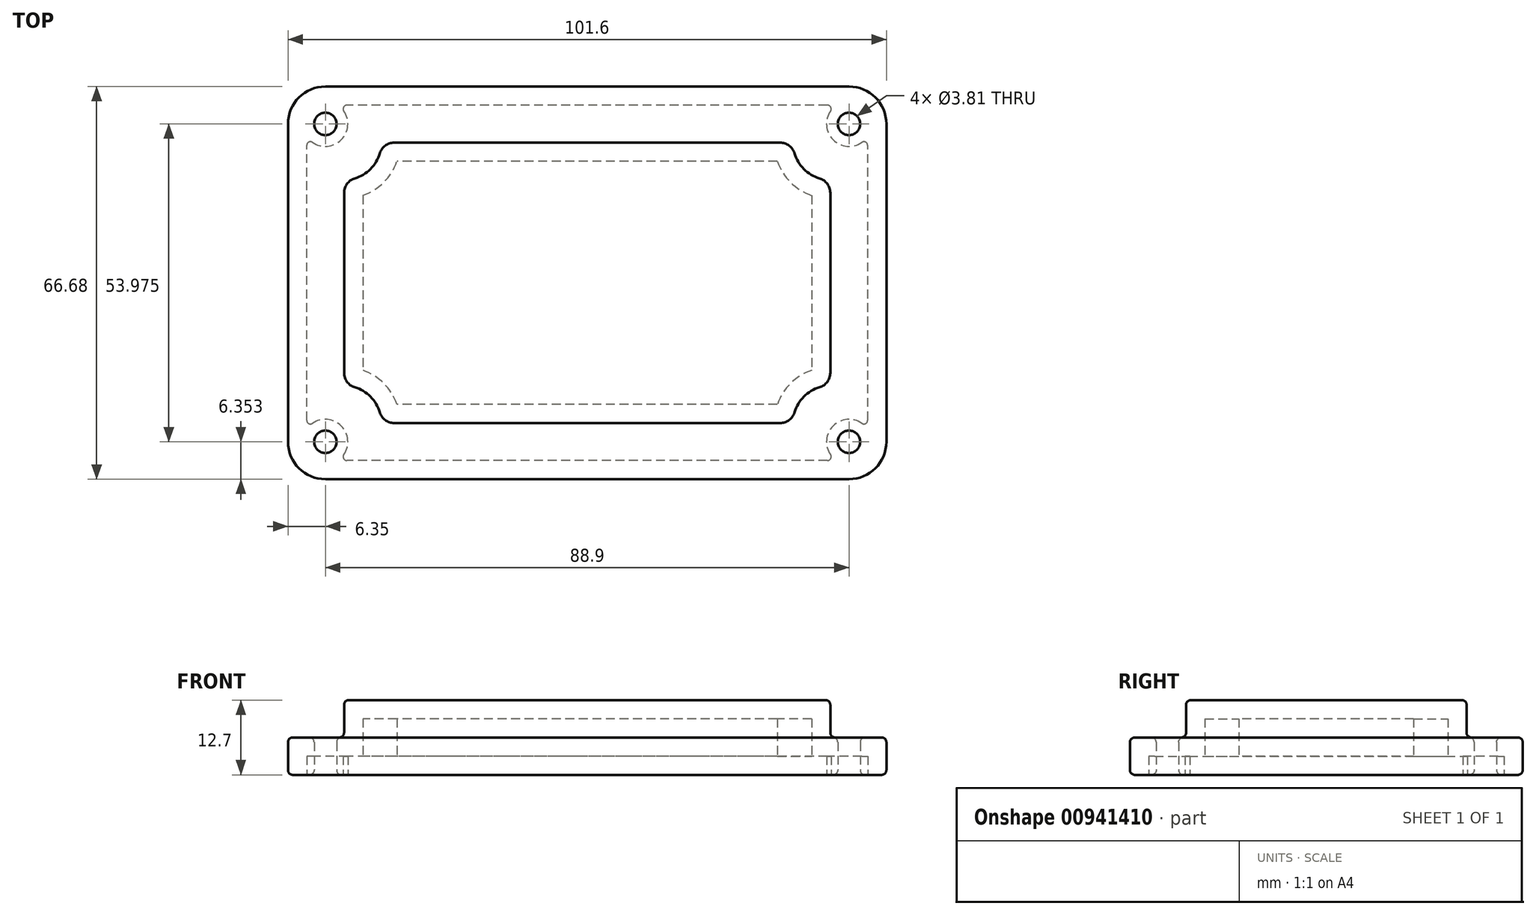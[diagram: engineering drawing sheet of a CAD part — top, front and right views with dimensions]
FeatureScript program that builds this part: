
annotation { "Feature Type Name" : "Feature", "Feature Type Description" : "" }
export const myFeature = defineFeature(function(context is Context, id is Id, definition is map)
    precondition{}
    {
        {
            var Q0;
            Q0=qCreatedBy(makeId("Top.planeOp"),FACE);
            var sketch = newSketch(context, id + "F0", { "sketchPlane" : qUnion([Q0])});
            skLineSegment(sketch, "E0.bottom", {"start": v(44.45, 33.34) * mm, "end": v(-44.45, 33.34) * mm});
            skLineSegment(sketch, "E0.top", {"start": v(44.45, -33.34) * mm, "end": v(-44.45, -33.34) * mm});
            skLineSegment(sketch, "E0.left", {"start": v(50.8, 26.99) * mm, "end": v(50.8, -26.99) * mm});
            skLineSegment(sketch, "E0.right", {"start": v(-50.8, 26.99) * mm, "end": v(-50.8, -26.99) * mm});
            skPoint(sketch, "E0.middle", {"position": v(0, 0) * mm});
            skPoint(sketch, "E1.visualSharp", {"position": v(-50.8, 33.34) * mm});
            skArc(sketch, "E1.filletArc", {"start": v(-44.45, 33.34) * mm, "mid": v(-48.94, 31.48) * mm, "end": v(-50.8, 26.99) * mm});
            skPoint(sketch, "E2.visualSharp", {"position": v(50.8, 33.34) * mm});
            skArc(sketch, "E2.filletArc", {"start": v(50.8, 26.99) * mm, "mid": v(48.94, 31.48) * mm, "end": v(44.45, 33.34) * mm});
            skPoint(sketch, "E3.visualSharp", {"position": v(50.8, -33.34) * mm});
            skArc(sketch, "E3.filletArc", {"start": v(44.45, -33.34) * mm, "mid": v(48.94, -31.48) * mm, "end": v(50.8, -26.99) * mm});
            skPoint(sketch, "E4.visualSharp", {"position": v(-50.8, -33.34) * mm});
            skArc(sketch, "E4.filletArc", {"start": v(-50.8, -26.99) * mm, "mid": v(-48.94, -31.48) * mm, "end": v(-44.45, -33.34) * mm});
            skSolve(sketch);
        }
        {
            var Q0;
            Q0 = qSketchRegion(id + "F0", true);
            extrude(context, id + "F1", {"entities" : qUnion([Q0]), "depth" : 6.35 * mm, "offsetDistance" : 25.4 * mm});
        }
        {
            var Q0;
            Q0=makeQuery(id+"F1.opExtrude","CAP_FACE",FACE,{"disambiguationData":[OSD([sQuery(id+"F0.wireOp",EDGE,"E0.bottom"),sQuery(id+"F0.wireOp",EDGE,"E0.top"),sQuery(id+"F0.wireOp",EDGE,"E0.left"),sQuery(id+"F0.wireOp",EDGE,"E0.right"),sQuery(id+"F0.wireOp",EDGE,"E1.filletArc"),sQuery(id+"F0.wireOp",EDGE,"E2.filletArc"),sQuery(id+"F0.wireOp",EDGE,"E3.filletArc"),sQuery(id+"F0.wireOp",EDGE,"E4.filletArc")])],"isStart":false});
            var sketch = newSketch(context, id + "F2", { "sketchPlane" : qUnion([Q0])});
            skLineSegment(sketch, "E5.bottom", {"start": v(32.76, 23.81) * mm, "end": v(-32.76, 23.81) * mm});
            skLineSegment(sketch, "E5.top", {"start": v(32.76, -23.81) * mm, "end": v(-32.76, -23.81) * mm});
            skLineSegment(sketch, "E5.left", {"start": v(41.28, 15.3) * mm, "end": v(41.28, -15.3) * mm});
            skLineSegment(sketch, "E5.right", {"start": v(-41.28, 15.3) * mm, "end": v(-41.28, -15.3) * mm});
            skPoint(sketch, "E5.middle", {"position": v(0, 0) * mm});
            skArc(sketch, "E6", {"start": v(-39.46, 17.73) * mm, "mid": v(-36.78, 19.32) * mm, "end": v(-35.19, 22) * mm});
            skArc(sketch, "E7", {"start": v(35.19, 22) * mm, "mid": v(36.78, 19.32) * mm, "end": v(39.46, 17.73) * mm});
            skArc(sketch, "E8", {"start": v(39.46, -17.73) * mm, "mid": v(36.78, -19.32) * mm, "end": v(35.19, -22) * mm});
            skArc(sketch, "E9", {"start": v(-35.19, -22) * mm, "mid": v(-36.78, -19.32) * mm, "end": v(-39.46, -17.73) * mm});
            skPoint(sketch, "E10.visualSharp", {"position": v(-41.28, 17.46) * mm});
            skArc(sketch, "E10.filletArc", {"start": v(-39.46, 17.73) * mm, "mid": v(-40.77, 16.81) * mm, "end": v(-41.28, 15.3) * mm});
            skPoint(sketch, "E11.visualSharp", {"position": v(-34.93, 23.81) * mm});
            skArc(sketch, "E11.filletArc", {"start": v(-32.76, 23.81) * mm, "mid": v(-34.27, 23.3) * mm, "end": v(-35.19, 22) * mm});
            skPoint(sketch, "E12.visualSharp", {"position": v(34.92, 23.81) * mm});
            skArc(sketch, "E12.filletArc", {"start": v(35.19, 22) * mm, "mid": v(34.27, 23.3) * mm, "end": v(32.76, 23.81) * mm});
            skPoint(sketch, "E13.visualSharp", {"position": v(41.28, 17.46) * mm});
            skArc(sketch, "E13.filletArc", {"start": v(41.28, 15.3) * mm, "mid": v(40.77, 16.81) * mm, "end": v(39.46, 17.73) * mm});
            skPoint(sketch, "E14.visualSharp", {"position": v(41.28, -17.46) * mm});
            skArc(sketch, "E14.filletArc", {"start": v(39.46, -17.73) * mm, "mid": v(40.77, -16.81) * mm, "end": v(41.28, -15.3) * mm});
            skPoint(sketch, "E15.visualSharp", {"position": v(34.93, -23.81) * mm});
            skArc(sketch, "E15.filletArc", {"start": v(32.76, -23.81) * mm, "mid": v(34.27, -23.3) * mm, "end": v(35.19, -22) * mm});
            skPoint(sketch, "E16.visualSharp", {"position": v(-34.93, -23.81) * mm});
            skArc(sketch, "E16.filletArc", {"start": v(-35.19, -22) * mm, "mid": v(-34.27, -23.3) * mm, "end": v(-32.76, -23.81) * mm});
            skPoint(sketch, "E17.visualSharp", {"position": v(-41.28, -17.46) * mm});
            skArc(sketch, "E17.filletArc", {"start": v(-41.27, -15.3) * mm, "mid": v(-40.77, -16.81) * mm, "end": v(-39.46, -17.73) * mm});
            skSolve(sketch);
        }
        {
            var Q0;
            Q0=makeQuery(id+"F2.imprint","IMPRINT",FACE,{"disambiguationData":[TD([[makeQuery(id+"F2.imprint","IMPRINT",EDGE,{"derivedFrom":sQuery(id+"F2.wireOp",EDGE,"E5.bottom")}),1.0]])]});
            extrude(context, id + "F3", {"entities" : qUnion([Q0]), "operationType" : NewBodyOperationType.ADD, "depth" : 6.35 * mm, "offsetDistance" : 25.4 * mm});
        }
        {
            var Q0;
            Q0=qCreatedBy(makeId("Top.planeOp"),FACE);
            var sketch = newSketch(context, id + "F4", { "sketchPlane" : qUnion([Q0])});
            skCircle(sketch, "E18", {"center": v(-44.45, 26.99) * mm, "radius": 1.9 * mm});
            skCircle(sketch, "E19", {"center": v(44.45, 26.99) * mm, "radius": 1.9 * mm});
            skCircle(sketch, "E20", {"center": v(44.45, -26.99) * mm, "radius": 1.9 * mm});
            skCircle(sketch, "E21", {"center": v(-44.45, -26.99) * mm, "radius": 1.9 * mm});
            skSolve(sketch);
        }
        {
            var Q0;
            Q0 = qSketchRegion(id + "F4", true);
            extrude(context, id + "F5", {"entities" : qUnion([Q0]), "operationType" : NewBodyOperationType.REMOVE, "endBound" : BoundingType.THROUGH_ALL, "depth" : 6.35 * mm, "offsetDistance" : 25.4 * mm});
        }
        {
            var Q0;
            Q0=makeQuery(id+"F1.opExtrude","CAP_FACE",FACE,{"disambiguationData":[OSD([sQuery(id+"F0.wireOp",EDGE,"E0.bottom"),sQuery(id+"F0.wireOp",EDGE,"E0.top"),sQuery(id+"F0.wireOp",EDGE,"E0.left"),sQuery(id+"F0.wireOp",EDGE,"E0.right"),sQuery(id+"F0.wireOp",EDGE,"E1.filletArc"),sQuery(id+"F0.wireOp",EDGE,"E2.filletArc"),sQuery(id+"F0.wireOp",EDGE,"E3.filletArc"),sQuery(id+"F0.wireOp",EDGE,"E4.filletArc")])],"isStart":false});
            var Q1;
            Q1=makeQuery(id+"F3.opExtrude","SWEPT_FACE",FACE,{"disambiguationData":[OSD([sQuery(id+"F2.wireOp",EDGE,"E15.filletArc")])]});
            var Q2;
            Q2=makeQuery(id+"F3.opExtrude","SWEPT_FACE",FACE,{"disambiguationData":[OSD([sQuery(id+"F2.wireOp",EDGE,"E13.filletArc")])]});
            var Q3;
            Q3=makeQuery(id+"F3.opExtrude","SWEPT_FACE",FACE,{"disambiguationData":[OSD([sQuery(id+"F2.wireOp",EDGE,"E14.filletArc")])]});
            var Q4;
            Q4=makeQuery(id+"F3.opExtrude","SWEPT_FACE",FACE,{"disambiguationData":[OSD([sQuery(id+"F2.wireOp",EDGE,"E5.bottom")])]});
            var Q5;
            Q5=makeQuery(id+"F3.opExtrude","CAP_FACE",FACE,{"disambiguationData":[OSD([sQuery(id+"F2.wireOp",EDGE,"E5.bottom"),sQuery(id+"F2.wireOp",EDGE,"E5.top"),sQuery(id+"F2.wireOp",EDGE,"E5.left"),sQuery(id+"F2.wireOp",EDGE,"E5.right"),sQuery(id+"F2.wireOp",EDGE,"E6"),sQuery(id+"F2.wireOp",EDGE,"E7"),sQuery(id+"F2.wireOp",EDGE,"E8"),sQuery(id+"F2.wireOp",EDGE,"E9"),sQuery(id+"F2.wireOp",EDGE,"E10.filletArc"),sQuery(id+"F2.wireOp",EDGE,"E11.filletArc"),sQuery(id+"F2.wireOp",EDGE,"E12.filletArc"),sQuery(id+"F2.wireOp",EDGE,"E13.filletArc"),sQuery(id+"F2.wireOp",EDGE,"E14.filletArc"),sQuery(id+"F2.wireOp",EDGE,"E15.filletArc"),sQuery(id+"F2.wireOp",EDGE,"E16.filletArc"),sQuery(id+"F2.wireOp",EDGE,"E17.filletArc")])],"isStart":false});
            var Q6;
            Q6=makeQuery(id+"F3.opExtrude","SWEPT_FACE",FACE,{"disambiguationData":[OSD([sQuery(id+"F2.wireOp",EDGE,"E5.top")])]});
            var Q7;
            Q7=makeQuery(id+"F3.opExtrude","SWEPT_FACE",FACE,{"disambiguationData":[OSD([sQuery(id+"F2.wireOp",EDGE,"E5.left")])]});
            var Q8;
            Q8=makeQuery(id+"F3.opExtrude","SWEPT_FACE",FACE,{"disambiguationData":[OSD([sQuery(id+"F2.wireOp",EDGE,"E5.right")])]});
            var Q9;
            Q9=makeQuery(id+"F3.opExtrude","SWEPT_FACE",FACE,{"disambiguationData":[OSD([sQuery(id+"F2.wireOp",EDGE,"E9")])]});
            var Q10;
            Q10=makeQuery(id+"F3.opExtrude","SWEPT_FACE",FACE,{"disambiguationData":[OSD([sQuery(id+"F2.wireOp",EDGE,"E10.filletArc")])]});
            var Q11;
            Q11=makeQuery(id+"F3.opExtrude","SWEPT_FACE",FACE,{"disambiguationData":[OSD([sQuery(id+"F2.wireOp",EDGE,"E11.filletArc")])]});
            var Q12;
            Q12=makeQuery(id+"F3.opExtrude","SWEPT_FACE",FACE,{"disambiguationData":[OSD([sQuery(id+"F2.wireOp",EDGE,"E12.filletArc")])]});
            var Q13;
            Q13=makeQuery(id+"F3.opExtrude","CAP_EDGE",EDGE,{"disambiguationData":[OSD([sQuery(id+"F2.wireOp",EDGE,"E8")])],"isStart":false});
            var Q14;
            Q14=makeQuery(id+"F3.opExtrude","CAP_EDGE",EDGE,{"disambiguationData":[OSD([sQuery(id+"F2.wireOp",EDGE,"E9")])],"isStart":false});
            var Q15;
            Q15=makeQuery(id+"F3.opExtrude","SWEPT_FACE",FACE,{"disambiguationData":[OSD([sQuery(id+"F2.wireOp",EDGE,"E16.filletArc")])]});
            var Q16;
            Q16=makeQuery(id+"F3.opExtrude","SWEPT_FACE",FACE,{"disambiguationData":[OSD([sQuery(id+"F2.wireOp",EDGE,"E17.filletArc")])]});
            var Q17;
            Q17=makeQuery(id+"F1.opExtrude","SWEPT_FACE",FACE,{"disambiguationData":[OSD([sQuery(id+"F0.wireOp",EDGE,"E0.bottom")])]});
            var Q18;
            Q18=makeQuery(id+"F1.opExtrude","SWEPT_FACE",FACE,{"disambiguationData":[OSD([sQuery(id+"F0.wireOp",EDGE,"E0.top")])]});
            var Q19;
            Q19=makeQuery(id+"F1.opExtrude","SWEPT_FACE",FACE,{"disambiguationData":[OSD([sQuery(id+"F0.wireOp",EDGE,"E0.left")])]});
            var Q20;
            Q20=makeQuery(id+"F1.opExtrude","SWEPT_FACE",FACE,{"disambiguationData":[OSD([sQuery(id+"F0.wireOp",EDGE,"E0.right")])]});
            var Q21;
            Q21=makeQuery(id+"F1.opExtrude","SWEPT_FACE",FACE,{"disambiguationData":[OSD([sQuery(id+"F0.wireOp",EDGE,"E1.filletArc")])]});
            var Q22;
            Q22=makeQuery(id+"F1.opExtrude","SWEPT_FACE",FACE,{"disambiguationData":[OSD([sQuery(id+"F0.wireOp",EDGE,"E2.filletArc")])]});
            var Q23;
            Q23=makeQuery(id+"F1.opExtrude","SWEPT_FACE",FACE,{"disambiguationData":[OSD([sQuery(id+"F0.wireOp",EDGE,"E3.filletArc")])]});
            var Q24;
            Q24=makeQuery(id+"F1.opExtrude","SWEPT_FACE",FACE,{"disambiguationData":[OSD([sQuery(id+"F0.wireOp",EDGE,"E4.filletArc")])]});
            var Q25;
            Q25=makeQuery(id+"F5.boolean.opBoolean","INTERSECT",EDGE,{"derivedFrom":[makeQuery(id+"F1.opExtrude","CAP_FACE",FACE,{"disambiguationData":[OSD([sQuery(id+"F0.wireOp",EDGE,"E0.bottom"),sQuery(id+"F0.wireOp",EDGE,"E0.top"),sQuery(id+"F0.wireOp",EDGE,"E0.left"),sQuery(id+"F0.wireOp",EDGE,"E0.right"),sQuery(id+"F0.wireOp",EDGE,"E1.filletArc"),sQuery(id+"F0.wireOp",EDGE,"E2.filletArc"),sQuery(id+"F0.wireOp",EDGE,"E3.filletArc"),sQuery(id+"F0.wireOp",EDGE,"E4.filletArc")])],"isStart":false}),makeQuery(id+"F5.opExtrude","SWEPT_FACE",FACE,{"disambiguationData":[OSD([sQuery(id+"F4.wireOp",EDGE,"E21")])]})]});
            var Q26;
            Q26=makeQuery(id+"F5.boolean.opBoolean","INTERSECT",EDGE,{"derivedFrom":[makeQuery(id+"F1.opExtrude","CAP_FACE",FACE,{"disambiguationData":[OSD([sQuery(id+"F0.wireOp",EDGE,"E0.bottom"),sQuery(id+"F0.wireOp",EDGE,"E0.top"),sQuery(id+"F0.wireOp",EDGE,"E0.left"),sQuery(id+"F0.wireOp",EDGE,"E0.right"),sQuery(id+"F0.wireOp",EDGE,"E1.filletArc"),sQuery(id+"F0.wireOp",EDGE,"E2.filletArc"),sQuery(id+"F0.wireOp",EDGE,"E3.filletArc"),sQuery(id+"F0.wireOp",EDGE,"E4.filletArc")])],"isStart":false}),makeQuery(id+"F5.opExtrude","SWEPT_FACE",FACE,{"disambiguationData":[OSD([sQuery(id+"F4.wireOp",EDGE,"E20")])]})]});
            var Q27;
            Q27=makeQuery(id+"F5.boolean.opBoolean","INTERSECT",EDGE,{"derivedFrom":[makeQuery(id+"F1.opExtrude","CAP_FACE",FACE,{"disambiguationData":[OSD([sQuery(id+"F0.wireOp",EDGE,"E0.bottom"),sQuery(id+"F0.wireOp",EDGE,"E0.top"),sQuery(id+"F0.wireOp",EDGE,"E0.left"),sQuery(id+"F0.wireOp",EDGE,"E0.right"),sQuery(id+"F0.wireOp",EDGE,"E1.filletArc"),sQuery(id+"F0.wireOp",EDGE,"E2.filletArc"),sQuery(id+"F0.wireOp",EDGE,"E3.filletArc"),sQuery(id+"F0.wireOp",EDGE,"E4.filletArc")])],"isStart":false}),makeQuery(id+"F5.opExtrude","SWEPT_FACE",FACE,{"disambiguationData":[OSD([sQuery(id+"F4.wireOp",EDGE,"E19")])]})]});
            var Q28;
            Q28=makeQuery(id+"F1.opExtrude","CAP_FACE",FACE,{"disambiguationData":[OSD([sQuery(id+"F0.wireOp",EDGE,"E0.bottom"),sQuery(id+"F0.wireOp",EDGE,"E0.top"),sQuery(id+"F0.wireOp",EDGE,"E0.left"),sQuery(id+"F0.wireOp",EDGE,"E0.right"),sQuery(id+"F0.wireOp",EDGE,"E1.filletArc"),sQuery(id+"F0.wireOp",EDGE,"E2.filletArc"),sQuery(id+"F0.wireOp",EDGE,"E3.filletArc"),sQuery(id+"F0.wireOp",EDGE,"E4.filletArc")])],"isStart":true});
            var Q29;
            Q29=makeQuery(id+"F5.boolean.opBoolean","INTERSECT",EDGE,{"derivedFrom":[makeQuery(id+"F1.opExtrude","CAP_FACE",FACE,{"disambiguationData":[OSD([sQuery(id+"F0.wireOp",EDGE,"E0.bottom"),sQuery(id+"F0.wireOp",EDGE,"E0.top"),sQuery(id+"F0.wireOp",EDGE,"E0.left"),sQuery(id+"F0.wireOp",EDGE,"E0.right"),sQuery(id+"F0.wireOp",EDGE,"E1.filletArc"),sQuery(id+"F0.wireOp",EDGE,"E2.filletArc"),sQuery(id+"F0.wireOp",EDGE,"E3.filletArc"),sQuery(id+"F0.wireOp",EDGE,"E4.filletArc")])],"isStart":false}),makeQuery(id+"F5.opExtrude","SWEPT_FACE",FACE,{"disambiguationData":[OSD([sQuery(id+"F4.wireOp",EDGE,"E18")])]})]});
            var Q30;
            Q30=makeQuery(id+"F5.boolean.opBoolean","COPY",FACE,{"derivedFrom":makeQuery(id+"F5.opExtrude","SWEPT_FACE",FACE,{"disambiguationData":[OSD([sQuery(id+"F4.wireOp",EDGE,"E19")])]})});
            var Q31;
            Q31=makeQuery(id+"F1.opExtrude","CAP_EDGE",EDGE,{"disambiguationData":[OSD([sQuery(id+"F0.wireOp",EDGE,"E1.filletArc")])],"isStart":false});
            var Q32;
            Q32=makeQuery(id+"F1.opExtrude","CAP_EDGE",EDGE,{"disambiguationData":[OSD([sQuery(id+"F0.wireOp",EDGE,"E2.filletArc")])],"isStart":false});
            var Q33;
            Q33=makeQuery(id+"F1.opExtrude","CAP_EDGE",EDGE,{"disambiguationData":[OSD([sQuery(id+"F0.wireOp",EDGE,"E3.filletArc")])],"isStart":false});
            var Q34;
            Q34=makeQuery(id+"F1.opExtrude","CAP_EDGE",EDGE,{"disambiguationData":[OSD([sQuery(id+"F0.wireOp",EDGE,"E4.filletArc")])],"isStart":false});
            var Q35;
            Q35=makeQuery(id+"F3.opExtrude","CAP_FACE",FACE,{"disambiguationData":[OSD([sQuery(id+"F2.wireOp",EDGE,"E5.bottom"),sQuery(id+"F2.wireOp",EDGE,"E5.top"),sQuery(id+"F2.wireOp",EDGE,"E5.left"),sQuery(id+"F2.wireOp",EDGE,"E5.right"),sQuery(id+"F2.wireOp",EDGE,"E6"),sQuery(id+"F2.wireOp",EDGE,"E7"),sQuery(id+"F2.wireOp",EDGE,"E8"),sQuery(id+"F2.wireOp",EDGE,"E9"),sQuery(id+"F2.wireOp",EDGE,"E10.filletArc"),sQuery(id+"F2.wireOp",EDGE,"E11.filletArc"),sQuery(id+"F2.wireOp",EDGE,"E12.filletArc"),sQuery(id+"F2.wireOp",EDGE,"E13.filletArc"),sQuery(id+"F2.wireOp",EDGE,"E14.filletArc"),sQuery(id+"F2.wireOp",EDGE,"E15.filletArc"),sQuery(id+"F2.wireOp",EDGE,"E16.filletArc"),sQuery(id+"F2.wireOp",EDGE,"E17.filletArc")])],"isStart":true});
            var Q36;
            Q36=makeQuery(id+"F3.opExtrude","SWEPT_FACE",FACE,{"disambiguationData":[OSD([sQuery(id+"F2.wireOp",EDGE,"E8")])]});
            var Q37;
            Q37=makeQuery(id+"F3.opExtrude","CAP_EDGE",EDGE,{"disambiguationData":[OSD([sQuery(id+"F2.wireOp",EDGE,"E16.filletArc")])],"isStart":false});
            var Q38;
            Q38=makeQuery(id+"F3.opExtrude","CAP_EDGE",EDGE,{"disambiguationData":[OSD([sQuery(id+"F2.wireOp",EDGE,"E9")])],"isStart":true});
            var Q39;
            Q39=makeQuery(id+"F3.opExtrude","CAP_EDGE",EDGE,{"disambiguationData":[OSD([sQuery(id+"F2.wireOp",EDGE,"E17.filletArc")])],"isStart":false});
            var Q40;
            Q40=makeQuery(id+"F3.opExtrude","CAP_EDGE",EDGE,{"disambiguationData":[OSD([sQuery(id+"F2.wireOp",EDGE,"E5.bottom")])],"isStart":false});
            var Q41;
            Q41=makeQuery(id+"F3.opExtrude","CAP_EDGE",EDGE,{"disambiguationData":[OSD([sQuery(id+"F2.wireOp",EDGE,"E10.filletArc")])],"isStart":false});
            var Q42;
            Q42=makeQuery(id+"F3.opExtrude","CAP_EDGE",EDGE,{"disambiguationData":[OSD([sQuery(id+"F2.wireOp",EDGE,"E5.top")])],"isStart":false});
            var Q43;
            Q43=makeQuery(id+"F3.opExtrude","CAP_EDGE",EDGE,{"disambiguationData":[OSD([sQuery(id+"F2.wireOp",EDGE,"E11.filletArc")])],"isStart":false});
            var Q44;
            Q44=makeQuery(id+"F3.opExtrude","CAP_EDGE",EDGE,{"disambiguationData":[OSD([sQuery(id+"F2.wireOp",EDGE,"E5.left")])],"isStart":false});
            var Q45;
            Q45=makeQuery(id+"F3.opExtrude","CAP_EDGE",EDGE,{"disambiguationData":[OSD([sQuery(id+"F2.wireOp",EDGE,"E12.filletArc")])],"isStart":false});
            var Q46;
            Q46=makeQuery(id+"F3.opExtrude","CAP_EDGE",EDGE,{"disambiguationData":[OSD([sQuery(id+"F2.wireOp",EDGE,"E5.right")])],"isStart":false});
            var Q47;
            Q47=makeQuery(id+"F3.opExtrude","CAP_EDGE",EDGE,{"disambiguationData":[OSD([sQuery(id+"F2.wireOp",EDGE,"E13.filletArc")])],"isStart":false});
            var Q48;
            Q48=makeQuery(id+"F3.opExtrude","CAP_EDGE",EDGE,{"disambiguationData":[OSD([sQuery(id+"F2.wireOp",EDGE,"E6")])],"isStart":false});
            var Q49;
            Q49=makeQuery(id+"F3.opExtrude","CAP_EDGE",EDGE,{"disambiguationData":[OSD([sQuery(id+"F2.wireOp",EDGE,"E14.filletArc")])],"isStart":false});
            var Q50;
            Q50=makeQuery(id+"F3.opExtrude","CAP_EDGE",EDGE,{"disambiguationData":[OSD([sQuery(id+"F2.wireOp",EDGE,"E7")])],"isStart":false});
            var Q51;
            Q51=makeQuery(id+"F3.opExtrude","CAP_EDGE",EDGE,{"disambiguationData":[OSD([sQuery(id+"F2.wireOp",EDGE,"E15.filletArc")])],"isStart":false});
            var Q52;
            Q52=makeQuery(id+"F1.opExtrude","CAP_EDGE",EDGE,{"disambiguationData":[OSD([sQuery(id+"F0.wireOp",EDGE,"E0.left")])],"isStart":false});
            var Q53;
            Q53=makeQuery(id+"F1.opExtrude","CAP_EDGE",EDGE,{"disambiguationData":[OSD([sQuery(id+"F0.wireOp",EDGE,"E0.right")])],"isStart":false});
            var Q54;
            Q54=makeQuery(id+"F1.opExtrude","CAP_EDGE",EDGE,{"disambiguationData":[OSD([sQuery(id+"F0.wireOp",EDGE,"E0.bottom")])],"isStart":false});
            var Q55;
            Q55=makeQuery(id+"F1.opExtrude","CAP_EDGE",EDGE,{"disambiguationData":[OSD([sQuery(id+"F0.wireOp",EDGE,"E0.top")])],"isStart":false});
            var Q56;
            Q56=makeQuery(id+"F5.boolean.opBoolean","COPY",FACE,{"derivedFrom":makeQuery(id+"F5.opExtrude","SWEPT_FACE",FACE,{"disambiguationData":[OSD([sQuery(id+"F4.wireOp",EDGE,"E21")])]})});
            var Q57;
            Q57=makeQuery(id+"F5.boolean.opBoolean","COPY",FACE,{"derivedFrom":makeQuery(id+"F5.opExtrude","SWEPT_FACE",FACE,{"disambiguationData":[OSD([sQuery(id+"F4.wireOp",EDGE,"E20")])]})});
            var Q58;
            Q58=makeQuery(id+"F5.boolean.opBoolean","COPY",EDGE,{"derivedFrom":makeQuery(id+"F5.opExtrude","CAP_EDGE",EDGE,{"disambiguationData":[OSD([sQuery(id+"F4.wireOp",EDGE,"E19")])],"isStart":true})});
            var Q59;
            Q59=makeQuery(id+"F1.opExtrude","CAP_EDGE",EDGE,{"disambiguationData":[OSD([sQuery(id+"F0.wireOp",EDGE,"E1.filletArc")])],"isStart":true});
            var Q60;
            Q60=makeQuery(id+"F1.opExtrude","CAP_EDGE",EDGE,{"disambiguationData":[OSD([sQuery(id+"F0.wireOp",EDGE,"E2.filletArc")])],"isStart":true});
            var Q61;
            Q61=makeQuery(id+"F1.opExtrude","CAP_EDGE",EDGE,{"disambiguationData":[OSD([sQuery(id+"F0.wireOp",EDGE,"E3.filletArc")])],"isStart":true});
            var Q62;
            Q62=makeQuery(id+"F1.opExtrude","CAP_EDGE",EDGE,{"disambiguationData":[OSD([sQuery(id+"F0.wireOp",EDGE,"E4.filletArc")])],"isStart":true});
            var Q63;
            Q63=makeQuery(id+"F5.boolean.opBoolean","COPY",FACE,{"derivedFrom":makeQuery(id+"F5.opExtrude","SWEPT_FACE",FACE,{"disambiguationData":[OSD([sQuery(id+"F4.wireOp",EDGE,"E18")])]})});
            var Q64;
            Q64=makeQuery(id+"F3.opExtrude","SWEPT_EDGE",EDGE,{"disambiguationData":[OSD([sQuery(id+"F2.wireOp",EDGE,"E8"),sQuery(id+"F2.wireOp",EDGE,"E15.filletArc")])]});
            var Q65;
            Q65=makeQuery(id+"F3.opExtrude","SWEPT_EDGE",EDGE,{"disambiguationData":[OSD([sQuery(id+"F2.wireOp",EDGE,"E9"),sQuery(id+"F2.wireOp",EDGE,"E16.filletArc")])]});
            var Q66;
            Q66=makeQuery(id+"F3.opExtrude","SWEPT_EDGE",EDGE,{"disambiguationData":[OSD([sQuery(id+"F2.wireOp",EDGE,"E9"),sQuery(id+"F2.wireOp",EDGE,"E17.filletArc")])]});
            var Q67;
            Q67=makeQuery(id+"F3.opExtrude","SWEPT_EDGE",EDGE,{"disambiguationData":[OSD([sQuery(id+"F2.wireOp",EDGE,"E5.bottom"),sQuery(id+"F2.wireOp",EDGE,"E12.filletArc")])]});
            var Q68;
            Q68=makeQuery(id+"F3.opExtrude","SWEPT_EDGE",EDGE,{"disambiguationData":[OSD([sQuery(id+"F2.wireOp",EDGE,"E5.bottom"),sQuery(id+"F2.wireOp",EDGE,"E11.filletArc")])]});
            var Q69;
            Q69=makeQuery(id+"F3.opExtrude","SWEPT_EDGE",EDGE,{"disambiguationData":[OSD([sQuery(id+"F2.wireOp",EDGE,"E5.top"),sQuery(id+"F2.wireOp",EDGE,"E15.filletArc")])]});
            var Q70;
            Q70=makeQuery(id+"F3.opExtrude","SWEPT_EDGE",EDGE,{"disambiguationData":[OSD([sQuery(id+"F2.wireOp",EDGE,"E5.top"),sQuery(id+"F2.wireOp",EDGE,"E16.filletArc")])]});
            var Q71;
            Q71=makeQuery(id+"F3.opExtrude","SWEPT_EDGE",EDGE,{"disambiguationData":[OSD([sQuery(id+"F2.wireOp",EDGE,"E5.left"),sQuery(id+"F2.wireOp",EDGE,"E13.filletArc")])]});
            var Q72;
            Q72=makeQuery(id+"F3.opExtrude","SWEPT_EDGE",EDGE,{"disambiguationData":[OSD([sQuery(id+"F2.wireOp",EDGE,"E5.left"),sQuery(id+"F2.wireOp",EDGE,"E14.filletArc")])]});
            var Q73;
            Q73=makeQuery(id+"F3.opExtrude","SWEPT_EDGE",EDGE,{"disambiguationData":[OSD([sQuery(id+"F2.wireOp",EDGE,"E5.right"),sQuery(id+"F2.wireOp",EDGE,"E10.filletArc")])]});
            var Q74;
            Q74=makeQuery(id+"F3.opExtrude","SWEPT_FACE",FACE,{"disambiguationData":[OSD([sQuery(id+"F2.wireOp",EDGE,"E6")])]});
            var Q75;
            Q75=makeQuery(id+"F3.opExtrude","SWEPT_EDGE",EDGE,{"disambiguationData":[OSD([sQuery(id+"F2.wireOp",EDGE,"E5.right"),sQuery(id+"F2.wireOp",EDGE,"E17.filletArc")])]});
            var Q76;
            Q76=makeQuery(id+"F3.opExtrude","SWEPT_FACE",FACE,{"disambiguationData":[OSD([sQuery(id+"F2.wireOp",EDGE,"E7")])]});
            var Q77;
            Q77=makeQuery(id+"F3.opExtrude","SWEPT_EDGE",EDGE,{"disambiguationData":[OSD([sQuery(id+"F2.wireOp",EDGE,"E6"),sQuery(id+"F2.wireOp",EDGE,"E10.filletArc")])]});
            var Q78;
            Q78=makeQuery(id+"F3.opExtrude","SWEPT_EDGE",EDGE,{"disambiguationData":[OSD([sQuery(id+"F2.wireOp",EDGE,"E6"),sQuery(id+"F2.wireOp",EDGE,"E11.filletArc")])]});
            var Q79;
            Q79=makeQuery(id+"F3.opExtrude","SWEPT_EDGE",EDGE,{"disambiguationData":[OSD([sQuery(id+"F2.wireOp",EDGE,"E7"),sQuery(id+"F2.wireOp",EDGE,"E12.filletArc")])]});
            var Q80;
            Q80=makeQuery(id+"F3.opExtrude","SWEPT_EDGE",EDGE,{"disambiguationData":[OSD([sQuery(id+"F2.wireOp",EDGE,"E7"),sQuery(id+"F2.wireOp",EDGE,"E13.filletArc")])]});
            var Q81;
            Q81=makeQuery(id+"F3.opExtrude","SWEPT_EDGE",EDGE,{"disambiguationData":[OSD([sQuery(id+"F2.wireOp",EDGE,"E8"),sQuery(id+"F2.wireOp",EDGE,"E14.filletArc")])]});
            var Q82;
            Q82=makeQuery(id+"F3.opExtrude","CAP_EDGE",EDGE,{"disambiguationData":[OSD([sQuery(id+"F2.wireOp",EDGE,"E17.filletArc")])],"isStart":true});
            var Q83;
            Q83=makeQuery(id+"F3.opExtrude","CAP_EDGE",EDGE,{"disambiguationData":[OSD([sQuery(id+"F2.wireOp",EDGE,"E5.bottom")])],"isStart":true});
            var Q84;
            Q84=makeQuery(id+"F3.opExtrude","CAP_EDGE",EDGE,{"disambiguationData":[OSD([sQuery(id+"F2.wireOp",EDGE,"E10.filletArc")])],"isStart":true});
            var Q85;
            Q85=makeQuery(id+"F3.opExtrude","CAP_EDGE",EDGE,{"disambiguationData":[OSD([sQuery(id+"F2.wireOp",EDGE,"E5.top")])],"isStart":true});
            var Q86;
            Q86=makeQuery(id+"F3.opExtrude","CAP_EDGE",EDGE,{"disambiguationData":[OSD([sQuery(id+"F2.wireOp",EDGE,"E11.filletArc")])],"isStart":true});
            var Q87;
            Q87=makeQuery(id+"F3.opExtrude","CAP_EDGE",EDGE,{"disambiguationData":[OSD([sQuery(id+"F2.wireOp",EDGE,"E5.left")])],"isStart":true});
            var Q88;
            Q88=makeQuery(id+"F3.opExtrude","CAP_EDGE",EDGE,{"disambiguationData":[OSD([sQuery(id+"F2.wireOp",EDGE,"E12.filletArc")])],"isStart":true});
            var Q89;
            Q89=makeQuery(id+"F3.opExtrude","CAP_EDGE",EDGE,{"disambiguationData":[OSD([sQuery(id+"F2.wireOp",EDGE,"E5.right")])],"isStart":true});
            var Q90;
            Q90=makeQuery(id+"F3.opExtrude","CAP_EDGE",EDGE,{"disambiguationData":[OSD([sQuery(id+"F2.wireOp",EDGE,"E13.filletArc")])],"isStart":true});
            var Q91;
            Q91=makeQuery(id+"F3.opExtrude","CAP_EDGE",EDGE,{"disambiguationData":[OSD([sQuery(id+"F2.wireOp",EDGE,"E14.filletArc")])],"isStart":true});
            var Q92;
            Q92=makeQuery(id+"F3.opExtrude","CAP_EDGE",EDGE,{"disambiguationData":[OSD([sQuery(id+"F2.wireOp",EDGE,"E15.filletArc")])],"isStart":true});
            var Q93;
            Q93=makeQuery(id+"F3.opExtrude","CAP_EDGE",EDGE,{"disambiguationData":[OSD([sQuery(id+"F2.wireOp",EDGE,"E8")])],"isStart":true});
            var Q94;
            Q94=makeQuery(id+"F3.opExtrude","CAP_EDGE",EDGE,{"disambiguationData":[OSD([sQuery(id+"F2.wireOp",EDGE,"E16.filletArc")])],"isStart":true});
            var Q95;
            Q95=makeQuery(id+"F1.opExtrude","CAP_EDGE",EDGE,{"disambiguationData":[OSD([sQuery(id+"F0.wireOp",EDGE,"E0.right")])],"isStart":true});
            var Q96;
            Q96=makeQuery(id+"F1.opExtrude","SWEPT_EDGE",EDGE,{"disambiguationData":[OSD([sQuery(id+"F0.wireOp",EDGE,"E0.bottom"),sQuery(id+"F0.wireOp",EDGE,"E2.filletArc")])]});
            var Q97;
            Q97=makeQuery(id+"F1.opExtrude","SWEPT_EDGE",EDGE,{"disambiguationData":[OSD([sQuery(id+"F0.wireOp",EDGE,"E0.bottom"),sQuery(id+"F0.wireOp",EDGE,"E1.filletArc")])]});
            var Q98;
            Q98=makeQuery(id+"F1.opExtrude","SWEPT_EDGE",EDGE,{"disambiguationData":[OSD([sQuery(id+"F0.wireOp",EDGE,"E0.top"),sQuery(id+"F0.wireOp",EDGE,"E3.filletArc")])]});
            var Q99;
            Q99=makeQuery(id+"F5.boolean.opBoolean","COPY",EDGE,{"derivedFrom":makeQuery(id+"F5.opExtrude","CAP_EDGE",EDGE,{"disambiguationData":[OSD([sQuery(id+"F4.wireOp",EDGE,"E18")])],"isStart":true})});
            var Q100;
            Q100=makeQuery(id+"F1.opExtrude","SWEPT_EDGE",EDGE,{"disambiguationData":[OSD([sQuery(id+"F0.wireOp",EDGE,"E0.top"),sQuery(id+"F0.wireOp",EDGE,"E4.filletArc")])]});
            var Q101;
            Q101=makeQuery(id+"F1.opExtrude","SWEPT_EDGE",EDGE,{"disambiguationData":[OSD([sQuery(id+"F0.wireOp",EDGE,"E0.left"),sQuery(id+"F0.wireOp",EDGE,"E2.filletArc")])]});
            var Q102;
            Q102=makeQuery(id+"F1.opExtrude","SWEPT_EDGE",EDGE,{"disambiguationData":[OSD([sQuery(id+"F0.wireOp",EDGE,"E0.left"),sQuery(id+"F0.wireOp",EDGE,"E3.filletArc")])]});
            var Q103;
            Q103=makeQuery(id+"F1.opExtrude","SWEPT_EDGE",EDGE,{"disambiguationData":[OSD([sQuery(id+"F0.wireOp",EDGE,"E0.right"),sQuery(id+"F0.wireOp",EDGE,"E1.filletArc")])]});
            var Q104;
            Q104=makeQuery(id+"F1.opExtrude","SWEPT_EDGE",EDGE,{"disambiguationData":[OSD([sQuery(id+"F0.wireOp",EDGE,"E0.right"),sQuery(id+"F0.wireOp",EDGE,"E4.filletArc")])]});
            var Q105;
            Q105=makeQuery(id+"F1.opExtrude","CAP_EDGE",EDGE,{"disambiguationData":[OSD([sQuery(id+"F0.wireOp",EDGE,"E0.bottom")])],"isStart":true});
            var Q106;
            Q106=makeQuery(id+"F1.opExtrude","CAP_EDGE",EDGE,{"disambiguationData":[OSD([sQuery(id+"F0.wireOp",EDGE,"E0.top")])],"isStart":true});
            var Q107;
            Q107=makeQuery(id+"F1.opExtrude","CAP_EDGE",EDGE,{"disambiguationData":[OSD([sQuery(id+"F0.wireOp",EDGE,"E0.left")])],"isStart":true});
            var Q108;
            Q108=makeQuery(id+"F5.boolean.opBoolean","COPY",EDGE,{"derivedFrom":makeQuery(id+"F5.opExtrude","CAP_EDGE",EDGE,{"disambiguationData":[OSD([sQuery(id+"F4.wireOp",EDGE,"E21")])],"isStart":true})});
            var Q109;
            Q109=makeQuery(id+"F5.boolean.opBoolean","COPY",EDGE,{"derivedFrom":makeQuery(id+"F5.opExtrude","CAP_EDGE",EDGE,{"disambiguationData":[OSD([sQuery(id+"F4.wireOp",EDGE,"E20")])],"isStart":true})});
            var Q110;
            Q110=makeQuery(id+"F3.opExtrude","CAP_EDGE",EDGE,{"disambiguationData":[OSD([sQuery(id+"F2.wireOp",EDGE,"E6")])],"isStart":true});
            var Q111;
            Q111=makeQuery(id+"F3.opExtrude","CAP_EDGE",EDGE,{"disambiguationData":[OSD([sQuery(id+"F2.wireOp",EDGE,"E7")])],"isStart":true});
            fillet(context, id + "F6", {"entities" : qUnion([Q0, Q1, Q2, Q3, Q4, Q5, Q6, Q7, Q8, Q9, Q10, Q11, Q12, Q13, Q14, Q15, Q16, Q17, Q18, Q19, Q20, Q21, Q22, Q23, Q24, Q25, Q26, Q27, Q28, Q29, Q30, Q31, Q32, Q33, Q34, Q35, Q36, Q37, Q38, Q39, Q40, Q41, Q42, Q43, Q44, Q45, Q46, Q47, Q48, Q49, Q50, Q51, Q52, Q53, Q54, Q55, Q56, Q57, Q58, Q59, Q60, Q61, Q62, Q63, Q64, Q65, Q66, Q67, Q68, Q69, Q70, Q71, Q72, Q73, Q74, Q75, Q76, Q77, Q78, Q79, Q80, Q81, Q82, Q83, Q84, Q85, Q86, Q87, Q88, Q89, Q90, Q91, Q92, Q93, Q94, Q95, Q96, Q97, Q98, Q99, Q100, Q101, Q102, Q103, Q104, Q105, Q106, Q107, Q108, Q109, Q110, Q111]), "radius" : 0.81 * mm, "tangentPropagation" : true, "allowEdgeOverflow" : false});
        }
        {
            var Q0;
            Q0=qCreatedBy(makeId("Top.planeOp"),FACE);
            var sketch = newSketch(context, id + "F7", { "sketchPlane" : qUnion([Q0])});
            skLineSegment(sketch, "E22.bottom", {"start": v(40.8, -30.16) * mm, "end": v(-40.8, -30.16) * mm});
            skLineSegment(sketch, "E22.top", {"start": v(40.8, 30.16) * mm, "end": v(-40.8, 30.16) * mm});
            skLineSegment(sketch, "E22.left", {"start": v(47.63, -23.34) * mm, "end": v(47.63, 23.34) * mm});
            skLineSegment(sketch, "E22.right", {"start": v(-47.63, -23.34) * mm, "end": v(-47.63, 23.34) * mm});
            skPoint(sketch, "E22.middle", {"position": v(0, 0) * mm});
            skArc(sketch, "E23", {"start": v(-41.32, -29.16) * mm, "mid": v(-41.76, -24.3) * mm, "end": v(-46.63, -23.86) * mm});
            skArc(sketch, "E24", {"start": v(-46.63, 23.86) * mm, "mid": v(-41.76, 24.3) * mm, "end": v(-41.32, 29.16) * mm});
            skArc(sketch, "E25", {"start": v(46.63, -23.86) * mm, "mid": v(41.76, -24.3) * mm, "end": v(41.32, -29.16) * mm});
            skArc(sketch, "E26", {"start": v(41.32, 29.16) * mm, "mid": v(41.76, 24.3) * mm, "end": v(46.63, 23.86) * mm});
            skPoint(sketch, "E27.orphan", {"position": v(-47.63, -30.16) * mm});
            skPoint(sketch, "E28.orphan", {"position": v(47.63, -30.16) * mm});
            skPoint(sketch, "E29.orphan", {"position": v(47.63, 30.16) * mm});
            skPoint(sketch, "E30.orphan", {"position": v(-47.63, 30.16) * mm});
            skPoint(sketch, "E31.visualSharp", {"position": v(-42.34, 30.16) * mm});
            skArc(sketch, "E31.filletArc", {"start": v(-40.8, 30.16) * mm, "mid": v(-41.37, 29.82) * mm, "end": v(-41.32, 29.16) * mm});
            skPoint(sketch, "E32.visualSharp", {"position": v(-47.63, 24.88) * mm});
            skArc(sketch, "E32.filletArc", {"start": v(-46.63, 23.86) * mm, "mid": v(-47.28, 23.9) * mm, "end": v(-47.62, 23.34) * mm});
            skPoint(sketch, "E33.visualSharp", {"position": v(-47.63, -29.1) * mm});
            skArc(sketch, "E33.filletArc", {"start": v(-47.62, -23.34) * mm, "mid": v(-47.28, -23.9) * mm, "end": v(-46.63, -23.86) * mm});
            skPoint(sketch, "E34.visualSharp", {"position": v(-46.56, -30.16) * mm});
            skArc(sketch, "E34.filletArc", {"start": v(-41.32, -29.16) * mm, "mid": v(-41.37, -29.82) * mm, "end": v(-40.8, -30.16) * mm});
            skPoint(sketch, "E35.visualSharp", {"position": v(42.34, -30.16) * mm});
            skArc(sketch, "E35.filletArc", {"start": v(40.8, -30.16) * mm, "mid": v(41.37, -29.82) * mm, "end": v(41.32, -29.16) * mm});
            skPoint(sketch, "E36.visualSharp", {"position": v(47.63, -24.88) * mm});
            skArc(sketch, "E36.filletArc", {"start": v(46.63, -23.86) * mm, "mid": v(47.28, -23.9) * mm, "end": v(47.62, -23.34) * mm});
            skPoint(sketch, "E37.visualSharp", {"position": v(47.63, 29.1) * mm});
            skArc(sketch, "E37.filletArc", {"start": v(47.63, 23.34) * mm, "mid": v(47.28, 23.9) * mm, "end": v(46.63, 23.86) * mm});
            skPoint(sketch, "E38.visualSharp", {"position": v(46.56, 30.16) * mm});
            skArc(sketch, "E38.filletArc", {"start": v(41.32, 29.16) * mm, "mid": v(41.37, 29.82) * mm, "end": v(40.8, 30.16) * mm});
            skSolve(sketch);
        }
        {
            var Q0;
            Q0 = qSketchRegion(id + "F7", true);
            extrude(context, id + "F8", {"entities" : qUnion([Q0]), "operationType" : NewBodyOperationType.REMOVE, "depth" : 3.17 * mm, "offsetDistance" : 25.4 * mm});
        }
        {
            var Q0;
            Q0=makeQuery(id+"F8.boolean.opBoolean","COPY",FACE,{"derivedFrom":makeQuery(id+"F8.opExtrude","CAP_FACE",FACE,{"disambiguationData":[OSD([sQuery(id+"F7.wireOp",EDGE,"E22.bottom"),sQuery(id+"F7.wireOp",EDGE,"E22.top"),sQuery(id+"F7.wireOp",EDGE,"E22.left"),sQuery(id+"F7.wireOp",EDGE,"E22.right"),sQuery(id+"F7.wireOp",EDGE,"E23"),sQuery(id+"F7.wireOp",EDGE,"E24"),sQuery(id+"F7.wireOp",EDGE,"E25"),sQuery(id+"F7.wireOp",EDGE,"E26"),sQuery(id+"F7.wireOp",EDGE,"E31.filletArc"),sQuery(id+"F7.wireOp",EDGE,"E32.filletArc"),sQuery(id+"F7.wireOp",EDGE,"E33.filletArc"),sQuery(id+"F7.wireOp",EDGE,"E34.filletArc"),sQuery(id+"F7.wireOp",EDGE,"E35.filletArc"),sQuery(id+"F7.wireOp",EDGE,"E36.filletArc"),sQuery(id+"F7.wireOp",EDGE,"E37.filletArc"),sQuery(id+"F7.wireOp",EDGE,"E38.filletArc")])],"isStart":false})});
            var sketch = newSketch(context, id + "F9", { "sketchPlane" : qUnion([Q0])});
            skArc(sketch, "E39.0", {"start": v(38.1, 14.83) * mm, "mid": v(34.54, 17.08) * mm, "end": v(32.3, 20.64) * mm});
            skLineSegment(sketch, "E39.1", {"start": v(38.1, -14.83) * mm, "end": v(38.1, 14.83) * mm});
            skLineSegment(sketch, "E39.2", {"start": v(32.3, 20.64) * mm, "end": v(-32.3, 20.64) * mm});
            skArc(sketch, "E39.3", {"start": v(32.3, -20.64) * mm, "mid": v(34.54, -17.08) * mm, "end": v(38.1, -14.83) * mm});
            skArc(sketch, "E39.4", {"start": v(-32.3, 20.64) * mm, "mid": v(-34.54, 17.08) * mm, "end": v(-38.1, 14.83) * mm});
            skLineSegment(sketch, "E39.5", {"start": v(-38.1, -14.83) * mm, "end": v(-38.1, 14.83) * mm});
            skArc(sketch, "E39.6", {"start": v(-38.1, -14.83) * mm, "mid": v(-34.54, -17.08) * mm, "end": v(-32.3, -20.64) * mm});
            skLineSegment(sketch, "E39.7", {"start": v(32.3, -20.64) * mm, "end": v(-32.3, -20.64) * mm});
            skSolve(sketch);
        }
        {
            var Q0;
            Q0 = qSketchRegion(id + "F9", true);
            var Q1;
            Q1=makeQuery(id+"F3.opExtrude","CAP_FACE",FACE,{"disambiguationData":[OSD([sQuery(id+"F2.wireOp",EDGE,"E5.bottom"),sQuery(id+"F2.wireOp",EDGE,"E5.top"),sQuery(id+"F2.wireOp",EDGE,"E5.left"),sQuery(id+"F2.wireOp",EDGE,"E5.right"),sQuery(id+"F2.wireOp",EDGE,"E6"),sQuery(id+"F2.wireOp",EDGE,"E7"),sQuery(id+"F2.wireOp",EDGE,"E8"),sQuery(id+"F2.wireOp",EDGE,"E9"),sQuery(id+"F2.wireOp",EDGE,"E10.filletArc"),sQuery(id+"F2.wireOp",EDGE,"E11.filletArc"),sQuery(id+"F2.wireOp",EDGE,"E12.filletArc"),sQuery(id+"F2.wireOp",EDGE,"E13.filletArc"),sQuery(id+"F2.wireOp",EDGE,"E14.filletArc"),sQuery(id+"F2.wireOp",EDGE,"E15.filletArc"),sQuery(id+"F2.wireOp",EDGE,"E16.filletArc"),sQuery(id+"F2.wireOp",EDGE,"E17.filletArc")])],"isStart":false});
            extrude(context, id + "F10", {"entities" : qUnion([Q0]), "operationType" : NewBodyOperationType.REMOVE, "endBound" : BoundingType.UP_TO_SURFACE, "oppositeDirection" : true, "depth" : 8.64 * mm, "endBoundEntityFace" : qUnion([Q1]), "hasOffset" : true, "offsetDistance" : 3.17 * mm});
        }
    });
